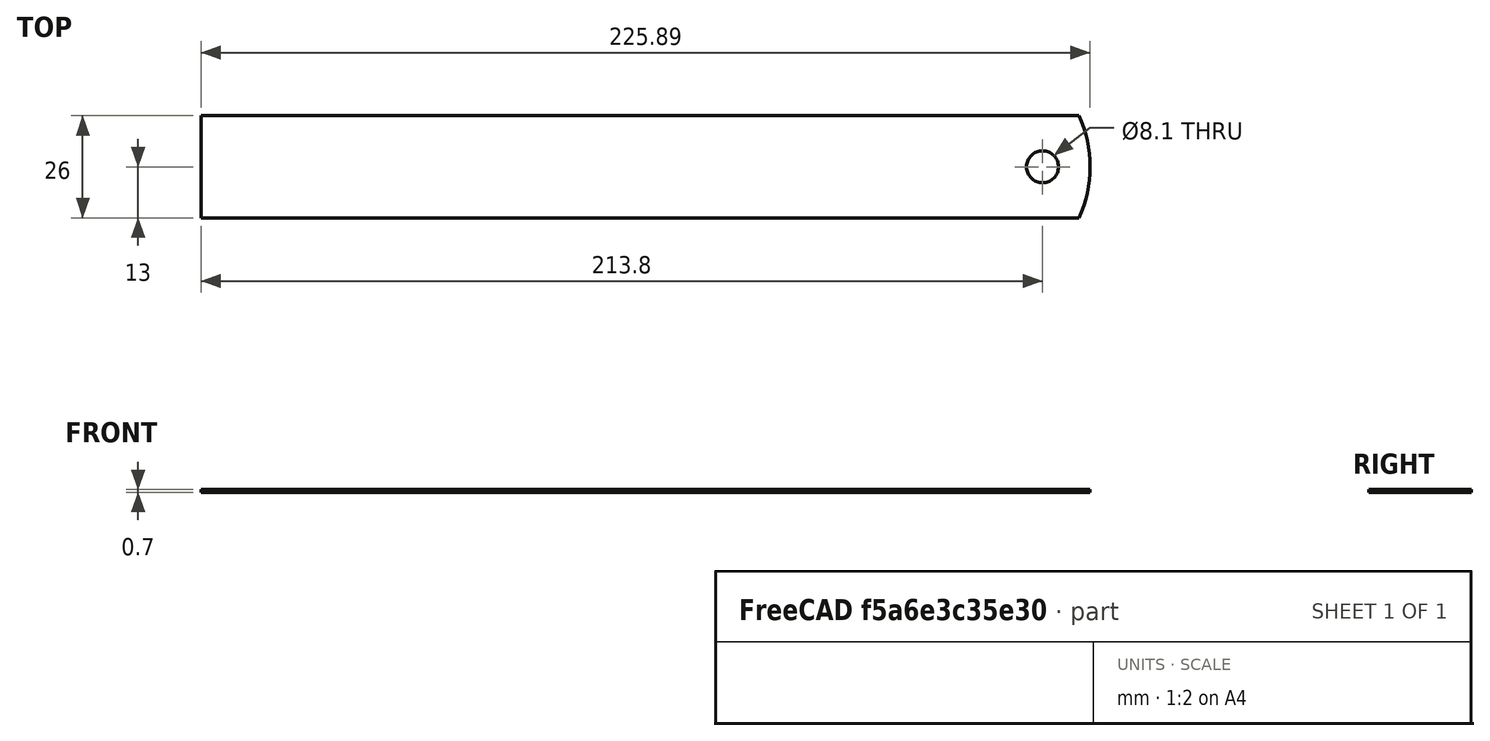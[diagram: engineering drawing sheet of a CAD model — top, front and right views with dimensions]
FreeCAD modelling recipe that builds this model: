
FCSTD DOCUMENT  (FreeCAD 0.19R24267 +148 (Git))
Label: reglet_003
License: Public Domain
LicenseURL: http://en.wikipedia.org/wiki/Public_domain
objects: Spreadsheet::Sheet×1, Sketcher::SketchObject×1, PartDesign::Pad×1, PartDesign::Body×1, App::Part×1
note: 4 computed .brp shape members not serialized (recipe doc carries the construction recipe); baked Part::Feature solids carry a one-line shape summary decoded from their .brp

FEATURE [Spreadsheet::Sheet] Spreadsheet001  label="regletSp"
  cells = A2=long; B2(long)=213.8; C2=axe trou; A3=larg; B3(larg)=26; A4=ep; B4(ep)=0.7; A5=trouDiam; B5(trouDiam)=8.1; A6=boutRayon; B6(boutRayon)=24
FEATURE [Sketcher::SketchObject] Sketch
  FullyConstrained = true
  MapMode = 5
  Support = -> [XY_Plane003]
  expr: Constraints[10] = <<regletSp>>.trouDiam
  expr: Constraints[9] = <<regletSp>>.long
  expr: Constraints[8] = <<regletSp>>.larg
  sketch-geometry (6):
    g0: Circle CenterX=213.8 CenterY=0 CenterZ=0 NormalX=0 NormalY=0 NormalZ=1 AngleXU=0 Radius=4.05
    g1: LineSegment StartX=223.054 StartY=13 StartZ=0 EndX=0 EndY=13 EndZ=0
    g2: LineSegment StartX=0 StartY=13 StartZ=0 EndX=0 EndY=-13 EndZ=0
    g3: LineSegment StartX=0 StartY=-13 StartZ=0 EndX=223.054 EndY=-13 EndZ=0
    g4: LineSegment StartX=223.054 StartY=13 StartZ=0 EndX=223.054 EndY=-13 EndZ=0
    g5: ArcOfCircle CenterX=194.68 CenterY=-5.5e-15 CenterZ=0 NormalX=0 NormalY=0 NormalZ=1 AngleXU=0 Radius=31.21 StartAngle=5.85356 EndAngle=6.71281
  constraints (17):
    c: PointOnObject(g0,g-1)
    c: Horizontal(g1)
    c: Coincident(g1,g2)
    c: Vertical(g2)
    c: Coincident(g2,g3)
    c: Horizontal(g3)
    c: Symmetric(g2,g1,g-1)
    c: Vertical(g4)
    c: DistanceY(g2,g2) = 26
    c: DistanceX(g2,g0) = 213.8
    c: Diameter(g0) = 8.1
    c: Coincident(g1,g4)
    c: Coincident(g3,g4)
    c: Coincident(g5,g1)
    c: Coincident(g5,g3)
    c: DistanceX(g-1,g5) = 194.68
    c: Diameter(g5) = 62.42
FEATURE [PartDesign::Pad] Pad
  Direction = (1,1,1)
  Length = 0.7
  Length2 = 100
  Profile = -> Sketch
  Type = 0
  expr: Length = <<regletSp>>.ep
FEATURE [PartDesign::Body] Body001  label="regletBdy"
  Group = -> [Sketch,Pad]
  Origin = -> Origin003
  Tip = -> Pad
FEATURE [App::Part] Part001  label="reglet"
  Group = -> [Body001,Spreadsheet001]
  Origin = -> Origin002
